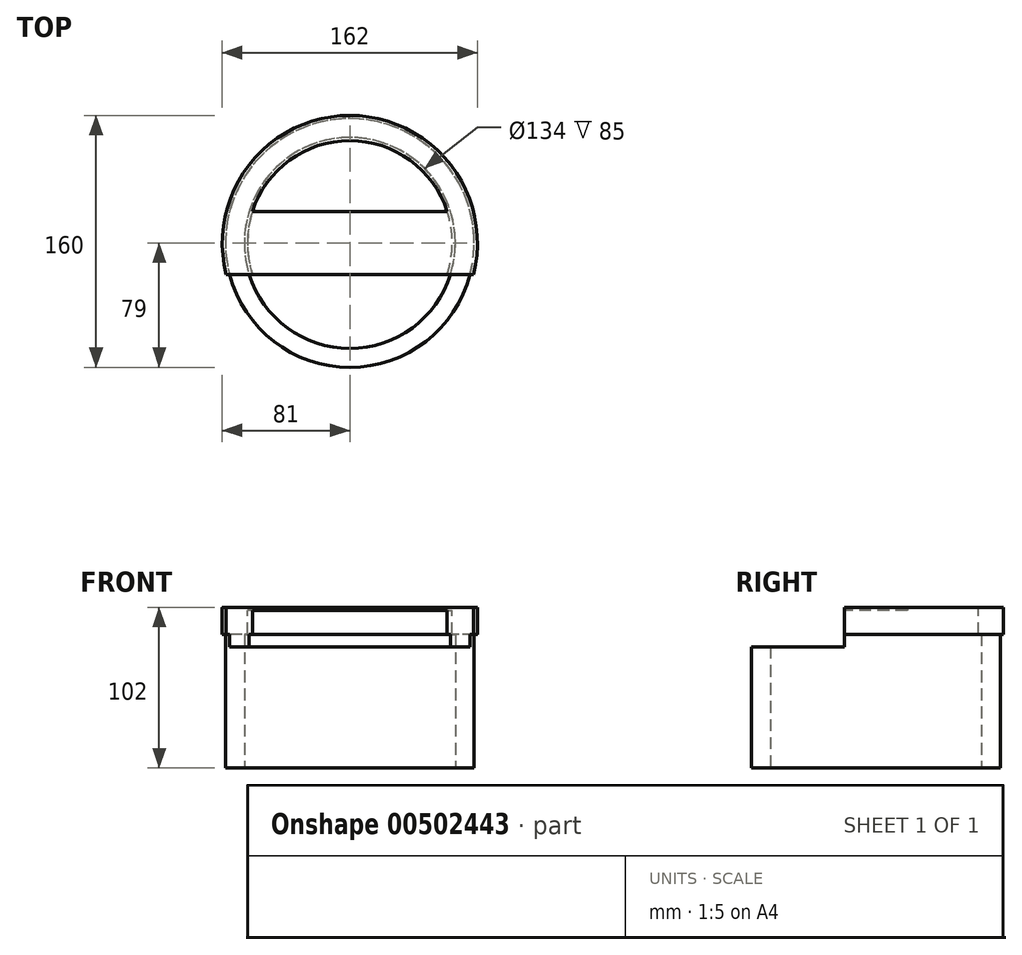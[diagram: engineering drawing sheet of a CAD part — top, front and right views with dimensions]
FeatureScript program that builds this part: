
annotation { "Feature Type Name" : "Feature", "Feature Type Description" : "" }
export const myFeature = defineFeature(function(context is Context, id is Id, definition is map)
    precondition{}
    {
        {
            var Q0;
            Q0=qCreatedBy(makeId("Top.planeOp"),FACE);
            var sketch = newSketch(context, id + "F0", { "sketchPlane" : qUnion([Q0])});
            skCircle(sketch, "E0", {"center": v(0, 0) * mm, "radius": 67 * mm});
            skCircle(sketch, "E1", {"center": v(0, 0) * mm, "radius": 79 * mm});
            skSolve(sketch);
        }
        {
            var Q0;
            Q0 = qSketchRegion(id + "F0", true);
            extrude(context, id + "F1", {"entities" : qUnion([Q0]), "depth" : 100 * mm});
        }
        {
            var Q0;
            Q0=makeQuery(id+"F1.opExtrude","CAP_FACE",FACE,{"disambiguationData":[OSD([sQuery(id+"F0.wireOp",EDGE,"E0"),sQuery(id+"F0.wireOp",EDGE,"E1")])],"isStart":false});
            var sketch = newSketch(context, id + "F2", { "sketchPlane" : qUnion([Q0])});
            skCircle(sketch, "E2.0", {"center": v(0, 0) * mm, "radius": 67 * mm});
            skCircle(sketch, "E3.0", {"center": v(0, 0) * mm, "radius": 79 * mm});
            skCircle(sketch, "E4", {"center": v(0, 0) * mm, "radius": 65 * mm});
            skCircle(sketch, "E5", {"center": v(0, 0) * mm, "radius": 81 * mm});
            skLineSegment(sketch, "E6", {"start": v(-61.85, 20) * mm, "end": v(61.85, 20) * mm});
            skLineSegment(sketch, "E7", {"start": v(-61.85, -20) * mm, "end": v(61.85, -20) * mm});
            skSolve(sketch);
        }
        {
            var Q0;
            Q0 = qSketchRegion(id + "F2", true);
            var Q1;
            Q1=makeQuery(id+"F2.imprint","IMPRINT",FACE,{"disambiguationData":[TD([[makeQuery(id+"F2.imprint","IMPRINT",EDGE,{"derivedFrom":sQuery(id+"F2.wireOp",EDGE,"E2.0")}),1.0]])]});
            extrude(context, id + "F3", {"entities" : qUnion([Q0, Q1]), "oppositeDirection" : true, "depth" : 15 * mm});
        }
        {
            var Q0;
            Q0 = qSketchRegion(id + "F2", true);
            var Q1;
            Q1=makeQuery(id+"F1.opExtrude","CAP_FACE",FACE,{"disambiguationData":[OSD([sQuery(id+"F0.wireOp",EDGE,"E0"),sQuery(id+"F0.wireOp",EDGE,"E1")])],"isStart":false});
            var Q2;
            Q2=makeQuery(id+"F2.imprint","IMPRINT",FACE,{"disambiguationData":[TD([[makeQuery(id+"F2.imprint","IMPRINT",EDGE,{"derivedFrom":sQuery(id+"F2.wireOp",EDGE,"E2.0")}),1.0]])]});
            var Q3;
            {var subQ0=sQuery(id+"F2.wireOp",EDGE,"E6");Q3=makeQuery(id+"F2.imprint","IMPRINT",FACE,{"disambiguationData":[TD([[makeQuery(id+"F2.imprint","IMPRINT",EDGE,{"derivedFrom":subQ0}),-1.0]])]});}
            extrude(context, id + "F4", {"entities" : qUnion([Q0, Q1, Q2, Q3]), "operationType" : NewBodyOperationType.ADD, "depth" : 2 * mm});
        }
        {
            var Q0;
            Q0=makeQuery(id+"F4.boolean.opBoolean","MERGE",FACE,{"derivedFrom":[makeQuery(id+"F4.opExtrude","CAP_FACE",FACE,{"disambiguationData":[OSD([sQuery(id+"F0.wireOp",EDGE,"E0"),sQuery(id+"F0.wireOp",EDGE,"E1")])],"isStart":false}),makeQuery(id+"F4.opExtrude","CAP_FACE",FACE,{"disambiguationData":[OSD([sQuery(id+"F2.wireOp",EDGE,"E2.0"),sQuery(id+"F2.wireOp",EDGE,"E4"),sQuery(id+"F2.wireOp",EDGE,"E6"),sQuery(id+"F2.wireOp",EDGE,"E7")])],"isStart":false}),makeQuery(id+"F4.opExtrude","CAP_FACE",FACE,{"disambiguationData":[OSD([sQuery(id+"F2.wireOp",EDGE,"E3.0"),sQuery(id+"F2.wireOp",EDGE,"E5")])],"isStart":false})]});
            var sketch = newSketch(context, id + "F5", { "sketchPlane" : qUnion([Q0])});
            skLineSegment(sketch, "E8.bottom", {"start": v(109.04, -20) * mm, "end": v(-82.01, -20) * mm});
            skLineSegment(sketch, "E8.top", {"start": v(109.04, -96.57) * mm, "end": v(-82.01, -96.57) * mm});
            skLineSegment(sketch, "E8.left", {"start": v(109.04, -20) * mm, "end": v(109.04, -96.57) * mm});
            skLineSegment(sketch, "E8.right", {"start": v(-82.01, -20) * mm, "end": v(-82.01, -96.57) * mm});
            skLineSegment(sketch, "E9.0", {"start": v(-61.85, -20) * mm, "end": v(61.85, -20) * mm});
            skSolve(sketch);
        }
        {
            var Q0;
            Q0 = qSketchRegion(id + "F5", true);
            extrude(context, id + "F6", {"entities" : qUnion([Q0]), "operationType" : NewBodyOperationType.REMOVE, "oppositeDirection" : true, "depth" : 25 * mm});
        }
    });
